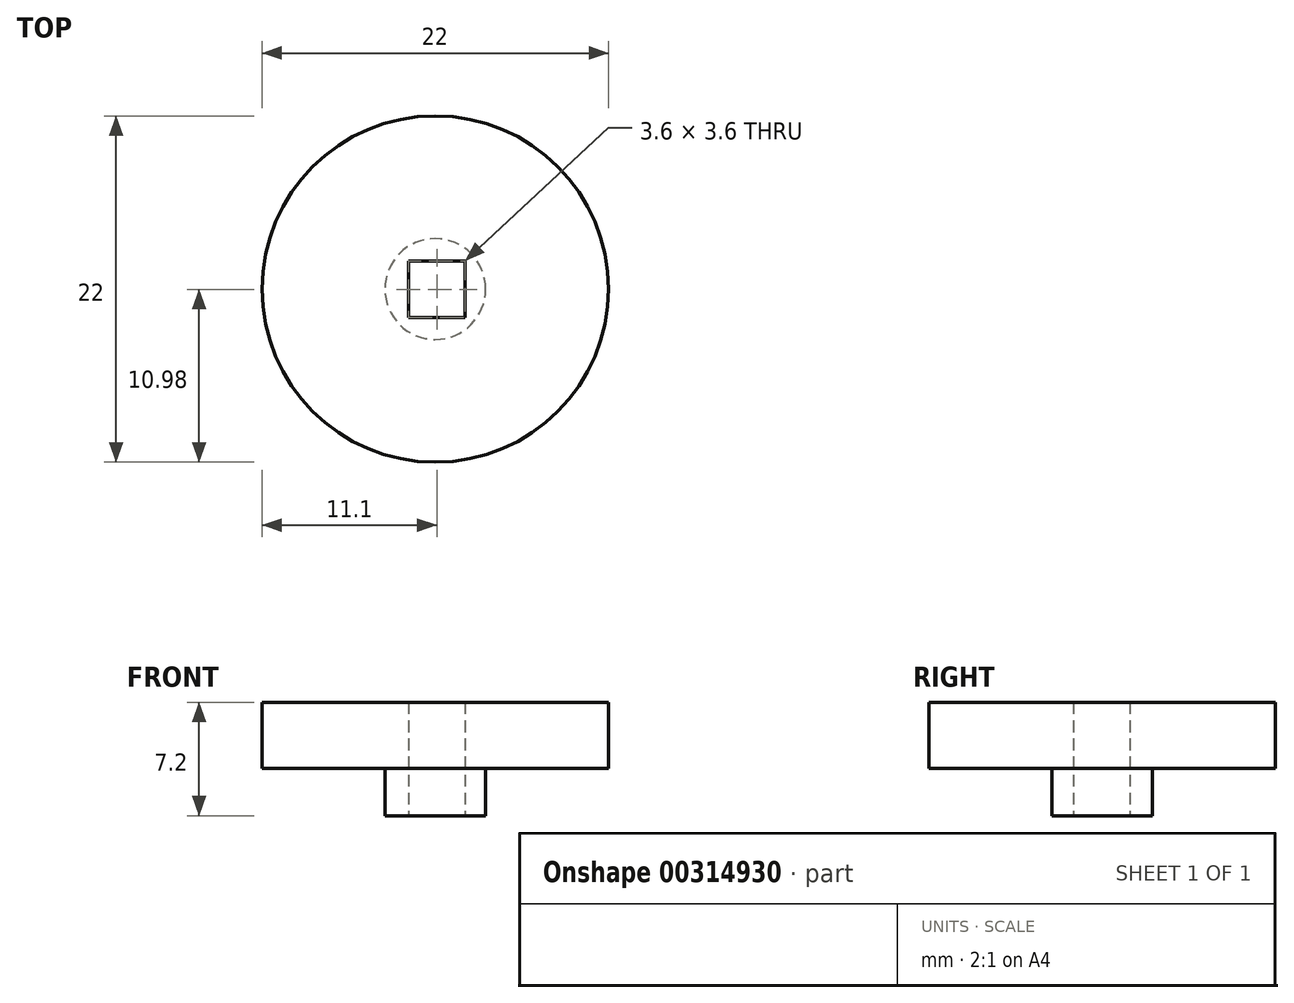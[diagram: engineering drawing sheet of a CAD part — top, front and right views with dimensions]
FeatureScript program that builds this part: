
annotation { "Feature Type Name" : "Feature", "Feature Type Description" : "" }
export const myFeature = defineFeature(function(context is Context, id is Id, definition is map)
    precondition{}
    {
        {
            var Q0;
            Q0=qCreatedBy(makeId("Top.planeOp"),FACE);
            var sketch = newSketch(context, id + "F0", { "sketchPlane" : qUnion([Q0])});
            skCircle(sketch, "E0", {"center": v(0, 0) * mm, "radius": 11 * mm});
            skSolve(sketch);
        }
        {
            var Q0;
            Q0 = qSketchRegion(id + "F0", true);
            extrude(context, id + "F1", {"entities" : qUnion([Q0]), "depth" : 4.2 * mm});
        }
        {
            var Q0;
            Q0=makeQuery(id+"F1.opExtrude","CAP_FACE",FACE,{"disambiguationData":[OSD([sQuery(id+"F0.wireOp",EDGE,"E0")])],"isStart":true});
            var sketch = newSketch(context, id + "F2", { "sketchPlane" : qUnion([Q0])});
            skLineSegment(sketch, "E1", {"start": v(0, 0) * mm, "end": v(11, 0) * mm});
            skLineSegment(sketch, "E2", {"start": v(0, 0) * mm, "end": v(7, -0.24) * mm});
            skLineSegment(sketch, "E3", {"start": v(0, 0) * mm, "end": v(7, 0.24) * mm});
            skLineSegment(sketch, "E4", {"start": v(0, 0) * mm, "end": v(10.72, 2.47) * mm});
            skLineSegment(sketch, "E5", {"start": v(0, 0) * mm, "end": v(10.72, -2.47) * mm});
            skArc(sketch, "E6", {"start": v(7, 0.24) * mm, "mid": v(7, 0.12) * mm, "end": v(7, 0) * mm});
            skArc(sketch, "E7", {"start": v(10.72, 2.47) * mm, "mid": v(11, 0) * mm, "end": v(10.72, -2.47) * mm});
            skLineSegment(sketch, "E8", {"start": v(7, -0.24) * mm, "end": v(10.72, -2.47) * mm});
            skLineSegment(sketch, "E9", {"start": v(7, 0.24) * mm, "end": v(10.72, 2.47) * mm});
            skLineSegment(sketch, "E10", {"start": v(7, -0.24) * mm, "end": v(7, 0) * mm});
            skLineSegment(sketch, "E11", {"start": v(8.34, 0) * mm, "end": v(8.28, 0.3) * mm});
            skSolve(sketch);
        }
        {
            var Q0;
            {var subQ4=sQuery(id+"F2.wireOp",EDGE,"E6");Q0=makeQuery(id+"F2.imprint","IMPRINT",FACE,{"disambiguationData":[TD([[makeQuery(id+"F2.imprint","IMPRINT",EDGE,{"derivedFrom":subQ4}),1.0]])]});}
            var Q1;
            {var subQ0=sQuery(id+"F2.wireOp",EDGE,"E8");Q1=makeQuery(id+"F2.imprint","IMPRINT",FACE,{"disambiguationData":[TD([[makeQuery(id+"F2.imprint","IMPRINT",EDGE,{"derivedFrom":subQ0}),1.0]])]});}
            extrude(context, id + "F3", {"entities" : qUnion([Q0, Q1]), "operationType" : NewBodyOperationType.REMOVE, "endBound" : BoundingType.THROUGH_ALL, "oppositeDirection" : true, "depth" : 25 * mm});
        }
        {
            var Q0;
            Q0=qCreatedBy(makeId("Right.planeOp"),FACE);
            var sketch = newSketch(context, id + "F4", { "sketchPlane" : qUnion([Q0])});
            skLineSegment(sketch, "E12", {"start": v(0, 0) * mm, "end": v(0, -12.66) * mm});
            skSolve(sketch);
        }
        {
            var Q0;
            Q0=makeQuery(id+"F1.opExtrude","CAP_FACE",FACE,{"disambiguationData":[OSD([sQuery(id+"F0.wireOp",EDGE,"E0")])],"isStart":true});
            var sketch = newSketch(context, id + "F5", { "sketchPlane" : qUnion([Q0])});
            skCircle(sketch, "E13", {"center": v(0, 0) * mm, "radius": 3.2 * mm});
            skSolve(sketch);
        }
        {
            var Q0;
            Q0 = qSketchRegion(id + "F5", true);
            extrude(context, id + "F6", {"entities" : qUnion([Q0]), "operationType" : NewBodyOperationType.ADD, "depth" : 3 * mm});
        }
        {
            var Q0;
            Q0=makeQuery(id+"F6.opExtrude","CAP_FACE",FACE,{"disambiguationData":[OSD([sQuery(id+"F5.wireOp",EDGE,"E13")])],"isStart":false});
            var sketch = newSketch(context, id + "F7", { "sketchPlane" : qUnion([Q0])});
            skLineSegment(sketch, "E14.bottom", {"start": v(1.9, 1.82) * mm, "end": v(-1.7, 1.82) * mm});
            skLineSegment(sketch, "E14.top", {"start": v(1.9, -1.78) * mm, "end": v(-1.7, -1.78) * mm});
            skLineSegment(sketch, "E14.left", {"start": v(1.9, 1.82) * mm, "end": v(1.9, -1.78) * mm});
            skLineSegment(sketch, "E14.right", {"start": v(-1.7, 1.82) * mm, "end": v(-1.7, -1.78) * mm});
            skPoint(sketch, "E14.middle", {"position": v(0.1, 0.02) * mm});
            skSolve(sketch);
        }
        {
            var Q0;
            Q0=makeQuery(id+"F7.imprint","IMPRINT",FACE,{"disambiguationData":[TD([[makeQuery(id+"F7.imprint","IMPRINT",EDGE,{"derivedFrom":sQuery(id+"F7.wireOp",EDGE,"E14.bottom")}),1.0]])]});
            extrude(context, id + "F8", {"entities" : qUnion([Q0]), "operationType" : NewBodyOperationType.REMOVE, "endBound" : BoundingType.THROUGH_ALL, "oppositeDirection" : true, "depth" : 25 * mm});
        }
    });
